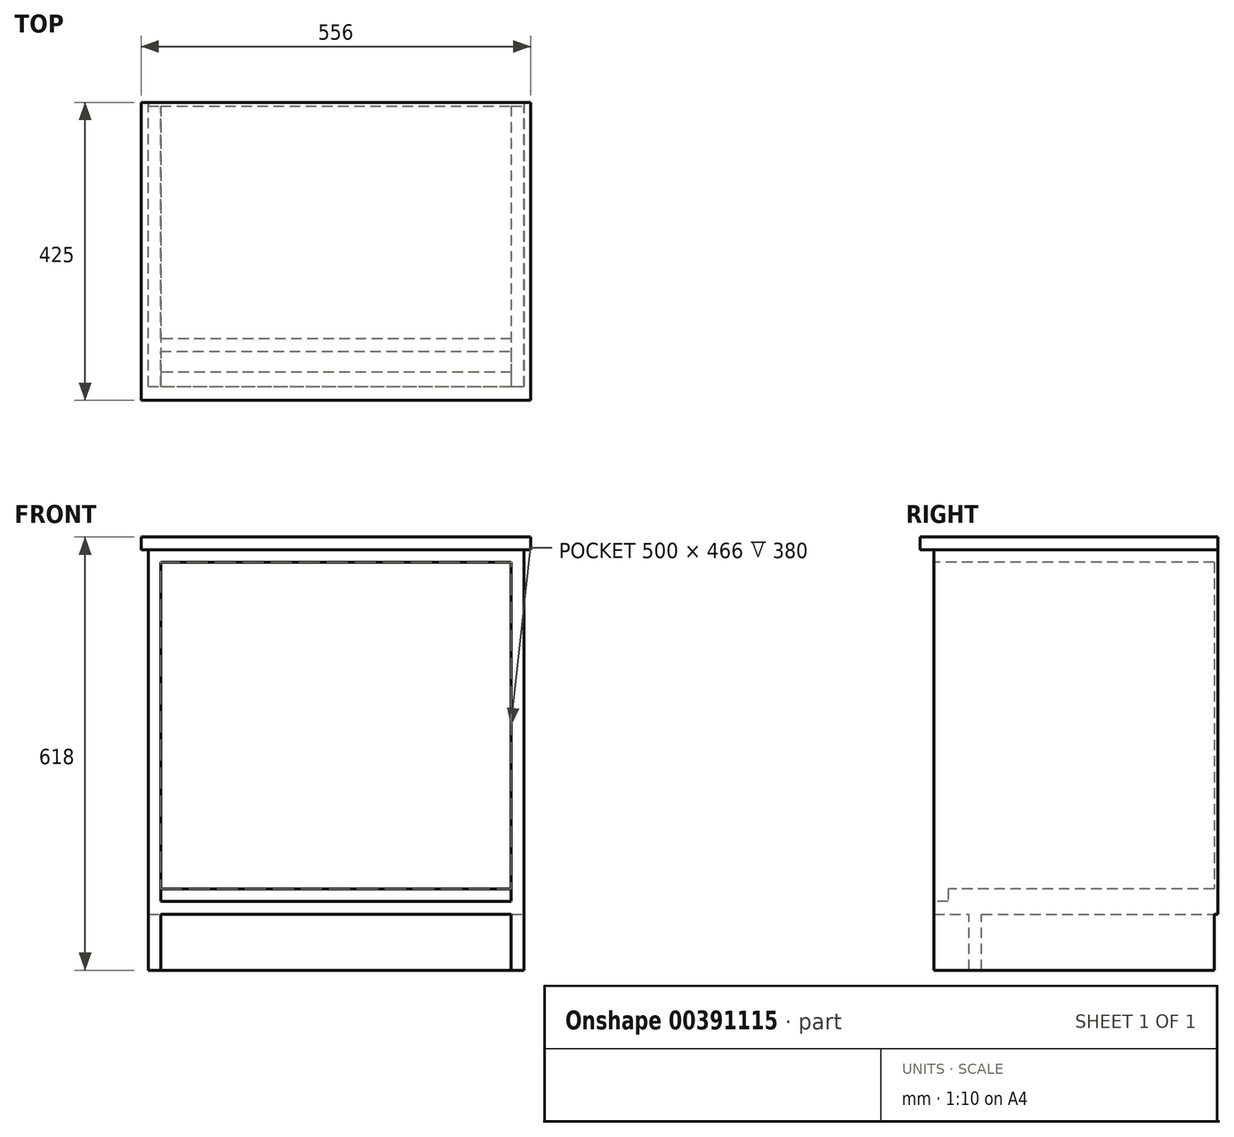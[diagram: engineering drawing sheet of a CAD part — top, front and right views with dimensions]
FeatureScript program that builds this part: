
annotation { "Feature Type Name" : "Feature", "Feature Type Description" : "" }
export const myFeature = defineFeature(function(context is Context, id is Id, definition is map)
    precondition{}
    {
        {
            assignVariable(context, id + "F0", {"name" : "WoodThickness", "anyValue" : 18 * mm});
        }
        {
            var Q0;
            Q0=qCreatedBy(makeId("Top.planeOp"),FACE);
            var sketch = newSketch(context, id + "F1", { "sketchPlane" : qUnion([Q0])});
            skLineSegment(sketch, "E0.bottom", {"start": v(0, 0) * mm, "end": v(536, 0) * mm});
            skLineSegment(sketch, "E0.top", {"start": v(0, 400) * mm, "end": v(536, 400) * mm});
            skLineSegment(sketch, "E0.left", {"start": v(0, 0) * mm, "end": v(0, 400) * mm});
            skLineSegment(sketch, "E0.right", {"start": v(536, 0) * mm, "end": v(536, 400) * mm});
            skSolve(sketch);
        }
        {
            var Q0;
            Q0=makeQuery(id+"F1.imprint","IMPRINT",FACE,{"disambiguationData":[TD([[makeQuery(id+"F1.imprint","IMPRINT",EDGE,{"derivedFrom":sQuery(id+"F1.wireOp",EDGE,"E0.bottom")}),1.0]])]});
            extrude(context, id + "F2", {"entities" : qUnion([Q0]), "depth" : getVariable(context, 'WoodThickness')});
        }
        {
            var Q0;
            Q0=makeQuery(id+"F2.opExtrude","CAP_FACE",FACE,{"disambiguationData":[OSD([sQuery(id+"F1.wireOp",EDGE,"E0.bottom"),sQuery(id+"F1.wireOp",EDGE,"E0.top"),sQuery(id+"F1.wireOp",EDGE,"E0.left"),sQuery(id+"F1.wireOp",EDGE,"E0.right")])],"isStart":false});
            var sketch = newSketch(context, id + "F3", { "sketchPlane" : qUnion([Q0])});
            skLineSegment(sketch, "E1.bottom", {"start": v(0, 400) * mm, "end": v(18, 400) * mm});
            skLineSegment(sketch, "E1.top", {"start": v(0, 0) * mm, "end": v(18, 0) * mm});
            skLineSegment(sketch, "E1.left", {"start": v(0, 400) * mm, "end": v(0, 0) * mm});
            skLineSegment(sketch, "E1.right", {"start": v(18, 400) * mm, "end": v(18, 0) * mm});
            skLineSegment(sketch, "E2.bottom", {"start": v(536, 400) * mm, "end": v(518, 400) * mm});
            skLineSegment(sketch, "E2.top", {"start": v(536, 0) * mm, "end": v(518, 0) * mm});
            skLineSegment(sketch, "E2.left", {"start": v(536, 400) * mm, "end": v(536, 0) * mm});
            skLineSegment(sketch, "E2.right", {"start": v(518, 400) * mm, "end": v(518, 0) * mm});
            skSolve(sketch);
        }
        {
            assignVariable(context, id + "F4", {"name" : "ToeKickHeight", "anyValue" : 80 * mm});
        }
        {
            var Q0;
            Q0 = qSketchRegion(id + "F3", true);
            extrude(context, id + "F5", {"entities" : qUnion([Q0]), "operationType" : NewBodyOperationType.ADD, "depth" : 600 * mm - getVariable(context, 'WoodThickness') * 2 - getVariable(context, 'ToeKickHeight')});
        }
        {
            var Q0;
            Q0=makeQuery(id+"F5.opExtrude","CAP_FACE",FACE,{"disambiguationData":[OSD([sQuery(id+"F3.wireOp",EDGE,"E1.bottom"),sQuery(id+"F3.wireOp",EDGE,"E1.top"),sQuery(id+"F3.wireOp",EDGE,"E1.left"),sQuery(id+"F3.wireOp",EDGE,"E1.right")])],"isStart":false});
            var sketch = newSketch(context, id + "F6", { "sketchPlane" : qUnion([Q0])});
            skLineSegment(sketch, "E3.bottom", {"start": v(0, 400) * mm, "end": v(536, 400) * mm});
            skLineSegment(sketch, "E3.top", {"start": v(0, 0) * mm, "end": v(536, 0) * mm});
            skLineSegment(sketch, "E3.left", {"start": v(0, 400) * mm, "end": v(0, 0) * mm});
            skLineSegment(sketch, "E3.right", {"start": v(536, 400) * mm, "end": v(536, 0) * mm});
            skSolve(sketch);
        }
        {
            var Q0;
            {var subQ2=sQuery(id+"F6.wireOp",EDGE,"E3.right");Q0=makeQuery(id+"F6.imprint","IMPRINT",FACE,{"disambiguationData":[TD([[makeQuery(id+"F6.imprint","IMPRINT",EDGE,{"derivedFrom":subQ2}),-1.0]])]});}
            var Q1;
            {var subQ0=sQuery(id+"F6.wireOp",EDGE,"E3.left");Q1=makeQuery(id+"F6.imprint","IMPRINT",FACE,{"disambiguationData":[TD([[makeQuery(id+"F6.imprint","IMPRINT",EDGE,{"derivedFrom":subQ0}),-1.0]])]});}
            extrude(context, id + "F7", {"entities" : qUnion([Q0, Q1]), "operationType" : NewBodyOperationType.ADD, "depth" : getVariable(context, 'WoodThickness')});
        }
        {
            var Q0;
            Q0=makeQuery(id+"F2.opExtrude","CAP_FACE",FACE,{"disambiguationData":[OSD([sQuery(id+"F1.wireOp",EDGE,"E0.bottom"),sQuery(id+"F1.wireOp",EDGE,"E0.top"),sQuery(id+"F1.wireOp",EDGE,"E0.left"),sQuery(id+"F1.wireOp",EDGE,"E0.right")])],"isStart":false});
            var sketch = newSketch(context, id + "F8", { "sketchPlane" : qUnion([Q0])});
            skLineSegment(sketch, "E4.bottom", {"start": v(518, 400) * mm, "end": v(18, 400) * mm});
            skLineSegment(sketch, "E4.top", {"start": v(518, 20) * mm, "end": v(18, 20) * mm});
            skLineSegment(sketch, "E4.left", {"start": v(518, 400) * mm, "end": v(518, 20) * mm});
            skLineSegment(sketch, "E4.right", {"start": v(18, 400) * mm, "end": v(18, 20) * mm});
            skPoint(sketch, "E5", {"position": v(518, 20) * mm});
            skSolve(sketch);
        }
        {
            var Q0;
            Q0 = qSketchRegion(id + "F8", true);
            extrude(context, id + "F9", {"entities" : qUnion([Q0]), "depth" : getVariable(context, 'WoodThickness')});
        }
        {
            var Q0;
            Q0=makeQuery(id+"F2.opExtrude","CAP_FACE",FACE,{"disambiguationData":[OSD([sQuery(id+"F1.wireOp",EDGE,"E0.bottom"),sQuery(id+"F1.wireOp",EDGE,"E0.top"),sQuery(id+"F1.wireOp",EDGE,"E0.left"),sQuery(id+"F1.wireOp",EDGE,"E0.right")])],"isStart":true});
            var sketch = newSketch(context, id + "F10", { "sketchPlane" : qUnion([Q0])});
            skLineSegment(sketch, "E6", {"start": v(0, -400) * mm, "end": v(0, 0) * mm});
            skLineSegment(sketch, "E7", {"start": v(536, 0) * mm, "end": v(536, -400) * mm});
            skLineSegment(sketch, "E8", {"start": v(536, -400) * mm, "end": v(518, -400) * mm});
            skLineSegment(sketch, "E9", {"start": v(518, -400) * mm, "end": v(518, -68) * mm});
            skLineSegment(sketch, "E10", {"start": v(518, -68) * mm, "end": v(18, -68) * mm});
            skLineSegment(sketch, "E11", {"start": v(18, -68) * mm, "end": v(18, -400) * mm});
            skLineSegment(sketch, "E12", {"start": v(18, -400) * mm, "end": v(0, -400) * mm});
            skLineSegment(sketch, "E13", {"start": v(0, 0) * mm, "end": v(18, 0) * mm});
            skLineSegment(sketch, "E14", {"start": v(18, 0) * mm, "end": v(18, -50) * mm});
            skLineSegment(sketch, "E15", {"start": v(18, -50) * mm, "end": v(518, -50) * mm});
            skLineSegment(sketch, "E16", {"start": v(518, -50) * mm, "end": v(518, 0) * mm});
            skLineSegment(sketch, "E17", {"start": v(518, 0) * mm, "end": v(536, 0) * mm});
            skSolve(sketch);
        }
        {
            var Q0;
            Q0=makeQuery(id+"F10.imprint","IMPRINT",FACE,{"disambiguationData":[TD([[makeQuery(id+"F10.imprint","IMPRINT",EDGE,{"derivedFrom":sQuery(id+"F10.wireOp",EDGE,"E6")}),1.0]])]});
            extrude(context, id + "F11", {"entities" : qUnion([Q0]), "operationType" : NewBodyOperationType.ADD, "depth" : getVariable(context, 'ToeKickHeight')});
        }
        {
            var Q0;
            Q0=makeQuery(id+"F11.boolean.opBoolean","MERGE",FACE,{"derivedFrom":[makeQuery(id+"F7.boolean.opBoolean","MERGE",FACE,{"derivedFrom":[makeQuery(id+"F5.boolean.opBoolean","MERGE",FACE,{"derivedFrom":[makeQuery(id+"F2.opExtrude","SWEPT_FACE",FACE,{"disambiguationData":[OSD([sQuery(id+"F1.wireOp",EDGE,"E0.top")])]}),makeQuery(id+"F5.opExtrude","SWEPT_FACE",FACE,{"disambiguationData":[OSD([sQuery(id+"F3.wireOp",EDGE,"E1.bottom")])]}),makeQuery(id+"F5.opExtrude","SWEPT_FACE",FACE,{"disambiguationData":[OSD([sQuery(id+"F3.wireOp",EDGE,"E2.bottom")])]})]}),makeQuery(id+"F7.opExtrude","SWEPT_FACE",FACE,{"disambiguationData":[OSD([sQuery(id+"F6.wireOp",EDGE,"E3.bottom")])]})]}),makeQuery(id+"F11.opExtrude","SWEPT_FACE",FACE,{"disambiguationData":[OSD([sQuery(id+"F10.wireOp",EDGE,"E8")])]}),makeQuery(id+"F11.opExtrude","SWEPT_FACE",FACE,{"disambiguationData":[OSD([sQuery(id+"F10.wireOp",EDGE,"E12")])]})]});
            var sketch = newSketch(context, id + "F12", { "sketchPlane" : qUnion([Q0])});
            skLineSegment(sketch, "E18.bottom", {"start": v(-536, 520) * mm, "end": v(0, 520) * mm});
            skLineSegment(sketch, "E18.top", {"start": v(-536, 0) * mm, "end": v(0, 0) * mm});
            skLineSegment(sketch, "E18.left", {"start": v(-536, 520) * mm, "end": v(-536, 0) * mm});
            skLineSegment(sketch, "E18.right", {"start": v(0, 520) * mm, "end": v(0, 0) * mm});
            skSolve(sketch);
        }
        {
            assignVariable(context, id + "F13", {"name" : "BackboardThickness", "anyValue" : 5 * mm});
        }
        {
            var Q0;
            Q0=makeQuery(id+"F12.imprint","IMPRINT",FACE,{"disambiguationData":[TD([[makeQuery(id+"F12.imprint","IMPRINT",EDGE,{"derivedFrom":sQuery(id+"F12.wireOp",EDGE,"E18.bottom")}),1.0]])]});
            var Q1;
            {var subQ0=sQuery(id+"F1.wireOp",EDGE,"E0.top");Q1=makeQuery(id+"F12.imprint","IMPRINT",FACE,{"disambiguationData":[TD([[makeQuery(id+"F12.imprint","IMPRINT",EDGE,{"derivedFrom":makeQuery(id+"F2.opExtrude","CAP_EDGE",EDGE,{"disambiguationData":[OSD([subQ0])],"isStart":false})}),-1.0]])]});}
            extrude(context, id + "F14", {"entities" : qUnion([Q0, Q1]), "operationType" : NewBodyOperationType.ADD, "depth" : getVariable(context, 'BackboardThickness')});
        }
        {
            var Q0;
            Q0=makeQuery(id+"F14.boolean.opBoolean","MERGE",FACE,{"derivedFrom":[makeQuery(id+"F7.opExtrude","CAP_FACE",FACE,{"disambiguationData":[OSD([sQuery(id+"F6.wireOp",EDGE,"E3.bottom"),sQuery(id+"F6.wireOp",EDGE,"E3.top"),sQuery(id+"F6.wireOp",EDGE,"E3.left"),sQuery(id+"F6.wireOp",EDGE,"E3.right")])],"isStart":false}),makeQuery(id+"F14.opExtrude","SWEPT_FACE",FACE,{"disambiguationData":[OSD([sQuery(id+"F12.wireOp",EDGE,"E18.bottom")])]})]});
            var sketch = newSketch(context, id + "F15", { "sketchPlane" : qUnion([Q0])});
            skLineSegment(sketch, "E19.bottom", {"start": v(-10, 405) * mm, "end": v(546, 405) * mm});
            skLineSegment(sketch, "E19.top", {"start": v(-10, -20) * mm, "end": v(546, -20) * mm});
            skLineSegment(sketch, "E19.left", {"start": v(-10, 405) * mm, "end": v(-10, -20) * mm});
            skLineSegment(sketch, "E19.right", {"start": v(546, 405) * mm, "end": v(546, -20) * mm});
            skSolve(sketch);
        }
        {
            var Q0;
            Q0 = qSketchRegion(id + "F15", true);
            extrude(context, id + "F16", {"entities" : qUnion([Q0]), "operationType" : NewBodyOperationType.ADD, "depth" : getVariable(context, 'WoodThickness')});
        }
    });
